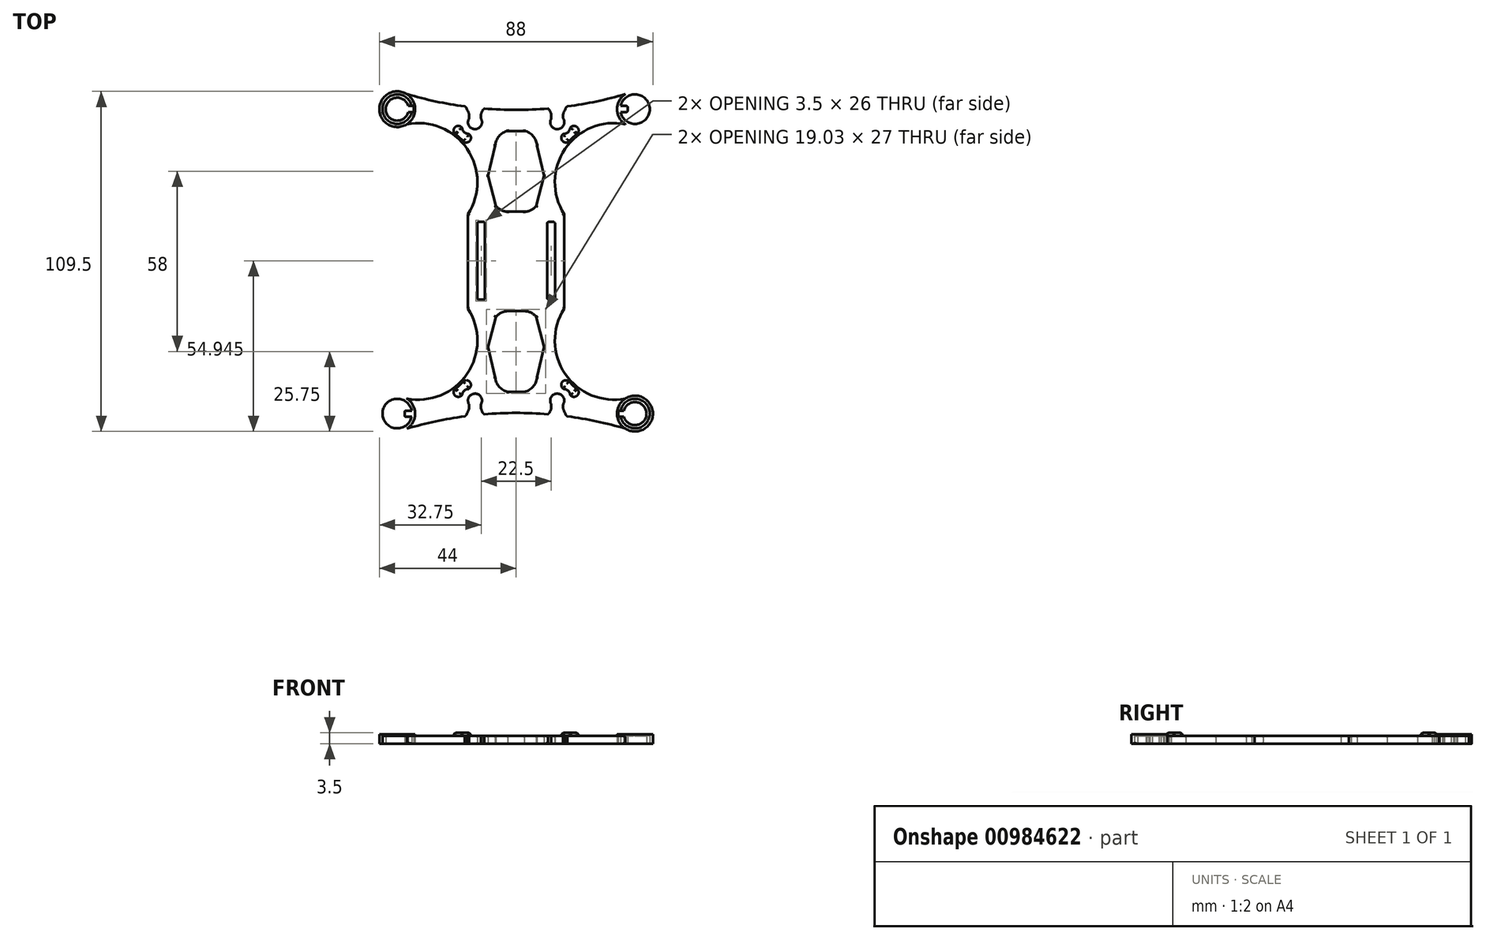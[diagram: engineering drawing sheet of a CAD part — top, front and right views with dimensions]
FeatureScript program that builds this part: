
annotation { "Feature Type Name" : "Feature", "Feature Type Description" : "" }
export const myFeature = defineFeature(function(context is Context, id is Id, definition is map)
    precondition{}
    {
        {
            var Q0;
            Q0=qCreatedBy(makeId("Top.planeOp"),FACE);
            var sketch = newSketch(context, id + "F0", { "sketchPlane" : qUnion([Q0])});
            skPoint(sketch, "E0.middle", {"position": v(0, 0) * mm});
            skCircle(sketch, "E1", {"center": v(-38.25, 49) * mm, "radius": 5.75 * mm});
            skCircle(sketch, "E2.MirrorC", {"center": v(38.25, 49) * mm, "radius": 5.75 * mm});
            skCircle(sketch, "E3.MirrorC", {"center": v(-38.25, -49) * mm, "radius": 5.75 * mm});
            skCircle(sketch, "E4.MirrorC", {"center": v(38.25, -49) * mm, "radius": 5.75 * mm});
            skArc(sketch, "E5", {"start": v(-35.12, 53.82) * mm, "mid": v(-25.9, 51.5) * mm, "end": v(-16.55, 49.89) * mm});
            skCircle(sketch, "E6", {"center": v(-38.25, 49) * mm, "radius": 3.7 * mm});
            skCircle(sketch, "E7.MirrorC", {"center": v(38.25, 49) * mm, "radius": 3.7 * mm});
            skCircle(sketch, "E8.MirrorC", {"center": v(38.25, -49) * mm, "radius": 3.7 * mm});
            skCircle(sketch, "E9.MirrorC", {"center": v(-38.25, -49) * mm, "radius": 3.7 * mm});
            skPoint(sketch, "E10.MirrorP", {"position": v(-9, -27.55) * mm});
            skArc(sketch, "E11.MirrorCS", {"start": v(-2.66, -42) * mm, "mid": v(-5.49, -40.33) * mm, "end": v(-6.7, -37.29) * mm});
            skArc(sketch, "E12.MirrorCS", {"start": v(-2.66, -16) * mm, "mid": v(-4.79, -16.51) * mm, "end": v(-6.5, -17.87) * mm});
            skLineSegment(sketch, "E13", {"start": v(-6.5, -17.87) * mm, "end": v(-9, -27.55) * mm});
            skLineSegment(sketch, "E14", {"start": v(-6.7, -37.29) * mm, "end": v(-9, -27.55) * mm});
            skArc(sketch, "E15.MirrorCS", {"start": v(2.66, -16) * mm, "mid": v(4.79, -16.51) * mm, "end": v(6.5, -17.87) * mm});
            skLineSegment(sketch, "E16.MirrorCS", {"start": v(6.5, -17.87) * mm, "end": v(9, -27.55) * mm});
            skLineSegment(sketch, "E17.MirrorCS", {"start": v(6.7, -37.29) * mm, "end": v(9, -27.55) * mm});
            skArc(sketch, "E18.MirrorCS", {"start": v(2.66, -42) * mm, "mid": v(5.49, -40.33) * mm, "end": v(6.7, -37.29) * mm});
            skLineSegment(sketch, "E19", {"start": v(-2.66, -16) * mm, "end": v(2.66, -16) * mm});
            skLineSegment(sketch, "E20", {"start": v(2.66, -42) * mm, "end": v(-2.66, -42) * mm});
            skLineSegment(sketch, "E21.MirrorCS", {"start": v(-2.66, 16) * mm, "end": v(2.66, 16) * mm});
            skArc(sketch, "E22.MirrorCS", {"start": v(-2.66, 16) * mm, "mid": v(-4.79, 16.51) * mm, "end": v(-6.5, 17.87) * mm});
            skLineSegment(sketch, "E23.MirrorCS", {"start": v(-6.5, 17.87) * mm, "end": v(-9, 27.55) * mm});
            skArc(sketch, "E24.MirrorCS", {"start": v(2.66, 16) * mm, "mid": v(4.79, 16.51) * mm, "end": v(6.5, 17.87) * mm});
            skLineSegment(sketch, "E25.MirrorCS", {"start": v(6.5, 17.87) * mm, "end": v(9, 27.55) * mm});
            skLineSegment(sketch, "E26.MirrorCS", {"start": v(-6.7, 37.29) * mm, "end": v(-9, 27.55) * mm});
            skLineSegment(sketch, "E27.MirrorCS", {"start": v(6.7, 37.29) * mm, "end": v(9, 27.55) * mm});
            skArc(sketch, "E28.MirrorCS", {"start": v(2.66, 42) * mm, "mid": v(5.49, 40.33) * mm, "end": v(6.7, 37.29) * mm});
            skLineSegment(sketch, "E29.MirrorCS", {"start": v(2.66, 42) * mm, "end": v(-2.66, 42) * mm});
            skArc(sketch, "E30.MirrorCS", {"start": v(-2.66, 42) * mm, "mid": v(-5.49, 40.33) * mm, "end": v(-6.7, 37.29) * mm});
            skArc(sketch, "E31", {"start": v(-15.5, 15.2) * mm, "mid": v(-15.74, 36.19) * mm, "end": v(-35.17, 44.14) * mm});
            skArc(sketch, "E32.MirrorCS", {"start": v(-35.12, -53.82) * mm, "mid": v(-25.9, -51.5) * mm, "end": v(-16.55, -49.89) * mm});
            skArc(sketch, "E33.MirrorCS", {"start": v(15.5, 15.2) * mm, "mid": v(15.74, 36.19) * mm, "end": v(35.17, 44.14) * mm});
            skArc(sketch, "E34.MirrorCS", {"start": v(15.5, -15.2) * mm, "mid": v(15.74, -36.19) * mm, "end": v(35.17, -44.14) * mm});
            skArc(sketch, "E35.MirrorCS", {"start": v(-15.5, -15.2) * mm, "mid": v(-15.74, -36.19) * mm, "end": v(-35.17, -44.14) * mm});
            skLineSegment(sketch, "E36", {"start": v(-15.5, -15.2) * mm, "end": v(-15.5, 15.2) * mm});
            skLineSegment(sketch, "E37.bottom", {"start": v(-12, -12.3) * mm, "end": v(-10.5, -12.3) * mm});
            skLineSegment(sketch, "E37.top", {"start": v(-12, 12.7) * mm, "end": v(-10.5, 12.7) * mm});
            skLineSegment(sketch, "E37.left", {"start": v(-12.5, -11.8) * mm, "end": v(-12.5, 12.2) * mm});
            skLineSegment(sketch, "E37.right", {"start": v(-10, -11.8) * mm, "end": v(-10, 12.2) * mm});
            skPoint(sketch, "E38.visualSharp", {"position": v(-10, -12.3) * mm});
            skArc(sketch, "E38.filletArc", {"start": v(-10.5, -12.3) * mm, "mid": v(-10.15, -12.16) * mm, "end": v(-10, -11.8) * mm});
            skPoint(sketch, "E39.visualSharp", {"position": v(-12.5, -12.3) * mm});
            skArc(sketch, "E39.filletArc", {"start": v(-12.5, -11.8) * mm, "mid": v(-12.35, -12.16) * mm, "end": v(-12, -12.3) * mm});
            skPoint(sketch, "E40.visualSharp", {"position": v(-10, 12.7) * mm});
            skArc(sketch, "E40.filletArc", {"start": v(-10, 12.2) * mm, "mid": v(-10.15, 12.55) * mm, "end": v(-10.5, 12.7) * mm});
            skPoint(sketch, "E41.visualSharp", {"position": v(-12.5, 12.7) * mm});
            skArc(sketch, "E41.filletArc", {"start": v(-12, 12.7) * mm, "mid": v(-12.35, 12.55) * mm, "end": v(-12.5, 12.2) * mm});
            skLineSegment(sketch, "E42.MirrorCS", {"start": v(12, -12.3) * mm, "end": v(10.5, -12.3) * mm});
            skArc(sketch, "E43.MirrorCS", {"start": v(12.5, -11.8) * mm, "mid": v(12.35, -12.16) * mm, "end": v(12, -12.3) * mm});
            skArc(sketch, "E44.MirrorCS", {"start": v(10.5, -12.3) * mm, "mid": v(10.15, -12.16) * mm, "end": v(10, -11.8) * mm});
            skLineSegment(sketch, "E45.MirrorCS", {"start": v(10, -11.8) * mm, "end": v(10, 12.2) * mm});
            skLineSegment(sketch, "E46.MirrorCS", {"start": v(12.5, -11.8) * mm, "end": v(12.5, 12.2) * mm});
            skArc(sketch, "E47.MirrorCS", {"start": v(10, 12.2) * mm, "mid": v(10.15, 12.55) * mm, "end": v(10.5, 12.7) * mm});
            skLineSegment(sketch, "E48.MirrorCS", {"start": v(12, 12.7) * mm, "end": v(10.5, 12.7) * mm});
            skArc(sketch, "E49.MirrorCS", {"start": v(12, 12.7) * mm, "mid": v(12.35, 12.55) * mm, "end": v(12.5, 12.2) * mm});
            skLineSegment(sketch, "E50", {"start": v(15.5, 15.2) * mm, "end": v(15.5, -15.2) * mm});
            skArc(sketch, "E51.trimOffspring", {"start": v(-10.28, 49.21) * mm, "mid": v(0, 48.79) * mm, "end": v(10.28, 49.21) * mm});
            skArc(sketch, "E52", {"start": v(-15.18, 45.95) * mm, "mid": v(-13.3, 42.57) * mm, "end": v(-11.24, 45.85) * mm});
            skArc(sketch, "E53", {"start": v(-15.18, 45.95) * mm, "mid": v(-15.18, 47.49) * mm, "end": v(-15.83, 48.88) * mm});
            skArc(sketch, "E54.MirrorCS", {"start": v(-11.24, 45.85) * mm, "mid": v(-11.2, 47.66) * mm, "end": v(-10.28, 49.21) * mm});
            skArc(sketch, "E55.trimOffspring", {"start": v(16.55, 49.89) * mm, "mid": v(25.9, 51.5) * mm, "end": v(35.12, 53.82) * mm});
            skArc(sketch, "E56.trimOffspring", {"start": v(-10.28, -49.21) * mm, "mid": v(0, -48.79) * mm, "end": v(10.28, -49.21) * mm});
            skArc(sketch, "E57.trimOffspring", {"start": v(16.55, -49.89) * mm, "mid": v(25.9, -51.5) * mm, "end": v(35.12, -53.82) * mm});
            skArc(sketch, "E58.MirrorCS", {"start": v(11.24, 45.85) * mm, "mid": v(11.2, 47.66) * mm, "end": v(10.28, 49.21) * mm});
            skArc(sketch, "E59.MirrorCS", {"start": v(15.18, 45.95) * mm, "mid": v(15.18, 47.49) * mm, "end": v(15.83, 48.88) * mm});
            skArc(sketch, "E60.MirrorCS", {"start": v(15.18, 45.95) * mm, "mid": v(13.3, 42.57) * mm, "end": v(11.24, 45.85) * mm});
            skArc(sketch, "E61.MirrorCS", {"start": v(15.18, -45.95) * mm, "mid": v(13.3, -42.57) * mm, "end": v(11.24, -45.85) * mm});
            skArc(sketch, "E62.MirrorCS", {"start": v(11.24, -45.85) * mm, "mid": v(11.2, -47.66) * mm, "end": v(10.28, -49.21) * mm});
            skArc(sketch, "E63.MirrorCS", {"start": v(15.18, -45.95) * mm, "mid": v(15.18, -47.49) * mm, "end": v(15.83, -48.88) * mm});
            skArc(sketch, "E64.MirrorCS", {"start": v(-11.24, -45.85) * mm, "mid": v(-11.2, -47.66) * mm, "end": v(-10.28, -49.21) * mm});
            skArc(sketch, "E65.MirrorCS", {"start": v(-15.18, -45.95) * mm, "mid": v(-15.18, -47.49) * mm, "end": v(-15.83, -48.88) * mm});
            skArc(sketch, "E66.MirrorCS", {"start": v(-15.18, -45.95) * mm, "mid": v(-13.3, -42.57) * mm, "end": v(-11.24, -45.85) * mm});
            skArc(sketch, "E67", {"start": v(16.55, 49.89) * mm, "mid": v(16.05, 49.49) * mm, "end": v(15.83, 48.88) * mm});
            skArc(sketch, "E68.MirrorCS", {"start": v(-16.55, 49.89) * mm, "mid": v(-16.05, 49.49) * mm, "end": v(-15.83, 48.88) * mm});
            skArc(sketch, "E69.MirrorCS", {"start": v(-16.55, -49.89) * mm, "mid": v(-16.05, -49.49) * mm, "end": v(-15.83, -48.88) * mm});
            skArc(sketch, "E70.MirrorCS", {"start": v(16.55, -49.89) * mm, "mid": v(16.05, -49.49) * mm, "end": v(15.83, -48.88) * mm});
            skCircle(sketch, "E71", {"center": v(-38.25, 49) * mm, "radius": 4.75 * mm});
            skCircle(sketch, "E72.MirrorC", {"center": v(38.25, 49) * mm, "radius": 4.75 * mm});
            skCircle(sketch, "E73.MirrorC", {"center": v(38.25, -49) * mm, "radius": 4.75 * mm});
            skCircle(sketch, "E74.MirrorC", {"center": v(-38.25, -49) * mm, "radius": 4.75 * mm});
            skSolve(sketch);
        }
        {
            var Q0;
            {var subQ4=sQuery(id+"F0.wireOp",EDGE,"E5");Q0=makeQuery(id+"F0.imprint","IMPRINT",FACE,{"disambiguationData":[TD([[makeQuery(id+"F0.imprint","IMPRINT",EDGE,{"derivedFrom":subQ4}),-1.0]])]});}
            var Q1;
            Q1=makeQuery(id+"F0.imprint","IMPRINT",FACE,{"disambiguationData":[TD([[makeQuery(id+"F0.imprint","IMPRINT",EDGE,{"derivedFrom":sQuery(id+"F0.wireOp",EDGE,"E9.MirrorC")}),1.0]])]});
            var Q2;
            Q2=makeQuery(id+"F0.imprint","IMPRINT",FACE,{"disambiguationData":[TD([[makeQuery(id+"F0.imprint","IMPRINT",EDGE,{"derivedFrom":sQuery(id+"F0.wireOp",EDGE,"E8.MirrorC")}),-1.0]])]});
            var Q3;
            Q3=makeQuery(id+"F0.imprint","IMPRINT",FACE,{"disambiguationData":[TD([[makeQuery(id+"F0.imprint","IMPRINT",EDGE,{"derivedFrom":sQuery(id+"F0.wireOp",EDGE,"E6")}),-1.0]])]});
            var Q4;
            Q4=makeQuery(id+"F0.imprint","IMPRINT",FACE,{"disambiguationData":[TD([[makeQuery(id+"F0.imprint","IMPRINT",EDGE,{"derivedFrom":sQuery(id+"F0.wireOp",EDGE,"E7.MirrorC")}),1.0]])]});
            var Q5;
            {var subQ0=sQuery(id+"F0.wireOp",EDGE,"7a08c846-7200-404a-ab22-a396ae0e95b40.MirrorCS");Q5=makeQuery(id+"F0.imprint","IMPRINT",FACE,{"disambiguationData":[TD([[makeQuery(id+"F0.imprint","IMPRINT",EDGE,{"derivedFrom":subQ0}),-1.0]])]});}
            extrude(context, id + "F1", {"entities" : qUnion([Q0, Q1, Q2, Q3, Q4, Q5]), "depth" : 2.5 * mm});
        }
        {
            var Q0;
            Q0=makeQuery(id+"F0.imprint","IMPRINT",FACE,{"disambiguationData":[TD([[makeQuery(id+"F0.imprint","IMPRINT",EDGE,{"derivedFrom":sQuery(id+"F0.wireOp",EDGE,"E71")}),-1.0]])]});
            var Q1;
            Q1=makeQuery(id+"F0.imprint","IMPRINT",FACE,{"disambiguationData":[TD([[makeQuery(id+"F0.imprint","IMPRINT",EDGE,{"derivedFrom":sQuery(id+"F0.wireOp",EDGE,"E72.MirrorC")}),1.0]])]});
            var Q2;
            Q2=makeQuery(id+"F0.imprint","IMPRINT",FACE,{"disambiguationData":[TD([[makeQuery(id+"F0.imprint","IMPRINT",EDGE,{"derivedFrom":sQuery(id+"F0.wireOp",EDGE,"E74.MirrorC")}),1.0]])]});
            var Q3;
            Q3=makeQuery(id+"F0.imprint","IMPRINT",FACE,{"disambiguationData":[TD([[makeQuery(id+"F0.imprint","IMPRINT",EDGE,{"derivedFrom":sQuery(id+"F0.wireOp",EDGE,"E73.MirrorC")}),-1.0]])]});
            extrude(context, id + "F2", {"entities" : qUnion([Q0, Q1, Q2, Q3]), "operationType" : NewBodyOperationType.ADD, "depth" : 3 * mm});
        }
        {
            var Q0;
            Q0=makeQuery(id+"F0.imprint","IMPRINT",FACE,{"disambiguationData":[TD([[makeQuery(id+"F0.imprint","IMPRINT",EDGE,{"derivedFrom":sQuery(id+"F0.wireOp",EDGE,"E6")}),1.0]])]});
            var Q1;
            Q1=makeQuery(id+"F0.imprint","IMPRINT",FACE,{"disambiguationData":[TD([[makeQuery(id+"F0.imprint","IMPRINT",EDGE,{"derivedFrom":sQuery(id+"F0.wireOp",EDGE,"E7.MirrorC")}),-1.0]])]});
            var Q2;
            Q2=makeQuery(id+"F0.imprint","IMPRINT",FACE,{"disambiguationData":[TD([[makeQuery(id+"F0.imprint","IMPRINT",EDGE,{"derivedFrom":sQuery(id+"F0.wireOp",EDGE,"E9.MirrorC")}),-1.0]])]});
            var Q3;
            Q3=makeQuery(id+"F0.imprint","IMPRINT",FACE,{"disambiguationData":[TD([[makeQuery(id+"F0.imprint","IMPRINT",EDGE,{"derivedFrom":sQuery(id+"F0.wireOp",EDGE,"E8.MirrorC")}),1.0]])]});
            extrude(context, id + "F3", {"entities" : qUnion([Q0, Q1, Q2, Q3]), "operationType" : NewBodyOperationType.REMOVE, "depth" : 6.5 * mm, "hasSecondDirection" : true, "secondDirectionOppositeDirection" : false, "secondDirectionDepth" : 2.5 * mm});
        }
        {
            var Q0;
            Q0=makeQuery(id+"F0.imprint","IMPRINT",FACE,{"disambiguationData":[TD([[makeQuery(id+"F0.imprint","IMPRINT",EDGE,{"derivedFrom":sQuery(id+"F0.wireOp",EDGE,"E6")}),-1.0]])]});
            var sketch = newSketch(context, id + "F4", { "sketchPlane" : qUnion([Q0])});
            skLineSegment(sketch, "E75.bottom", {"start": v(-33.4, 50.05) * mm, "end": v(-35.4, 50.05) * mm});
            skLineSegment(sketch, "E75.top", {"start": v(-33.4, 48.05) * mm, "end": v(-35.4, 48.05) * mm});
            skLineSegment(sketch, "E75.left", {"start": v(-32.9, 49.55) * mm, "end": v(-32.9, 48.55) * mm});
            skLineSegment(sketch, "E75.right", {"start": v(-35.9, 49.55) * mm, "end": v(-35.9, 48.55) * mm});
            skPoint(sketch, "E75.middle", {"position": v(-34.4, 49.05) * mm});
            skPoint(sketch, "E76.visualSharp", {"position": v(-32.9, 50.05) * mm});
            skArc(sketch, "E76.filletArc", {"start": v(-32.9, 49.55) * mm, "mid": v(-33.05, 49.9) * mm, "end": v(-33.4, 50.05) * mm});
            skPoint(sketch, "E77.visualSharp", {"position": v(-32.9, 48.05) * mm});
            skArc(sketch, "E77.filletArc", {"start": v(-33.4, 48.05) * mm, "mid": v(-33.05, 48.2) * mm, "end": v(-32.9, 48.55) * mm});
            skPoint(sketch, "E78.visualSharp", {"position": v(-35.9, 48.05) * mm});
            skArc(sketch, "E78.filletArc", {"start": v(-35.9, 48.55) * mm, "mid": v(-35.75, 48.2) * mm, "end": v(-35.4, 48.05) * mm});
            skPoint(sketch, "E79.visualSharp", {"position": v(-35.9, 50.05) * mm});
            skArc(sketch, "E79.filletArc", {"start": v(-35.4, 50.05) * mm, "mid": v(-35.75, 49.9) * mm, "end": v(-35.9, 49.55) * mm});
            skLineSegment(sketch, "E80.MirrorCS", {"start": v(33.4, 48.05) * mm, "end": v(35.4, 48.05) * mm});
            skLineSegment(sketch, "E81.MirrorCS", {"start": v(35.9, 49.55) * mm, "end": v(35.9, 48.55) * mm});
            skLineSegment(sketch, "E82.MirrorCS", {"start": v(33.4, 50.05) * mm, "end": v(35.4, 50.05) * mm});
            skLineSegment(sketch, "E83.MirrorCS", {"start": v(32.9, 49.55) * mm, "end": v(32.9, 48.55) * mm});
            skArc(sketch, "E84.MirrorCS", {"start": v(32.9, 49.55) * mm, "mid": v(33.05, 49.9) * mm, "end": v(33.4, 50.05) * mm});
            skArc(sketch, "E85.MirrorCS", {"start": v(33.4, 48.05) * mm, "mid": v(33.05, 48.2) * mm, "end": v(32.9, 48.55) * mm});
            skArc(sketch, "E86.MirrorCS", {"start": v(35.9, 48.55) * mm, "mid": v(35.75, 48.2) * mm, "end": v(35.4, 48.05) * mm});
            skArc(sketch, "E87.MirrorCS", {"start": v(35.4, 50.05) * mm, "mid": v(35.75, 49.9) * mm, "end": v(35.9, 49.55) * mm});
            skLineSegment(sketch, "E88.MirrorCS", {"start": v(33.4, -48.05) * mm, "end": v(35.4, -48.05) * mm});
            skLineSegment(sketch, "E89.MirrorCS", {"start": v(33.4, -50.05) * mm, "end": v(35.4, -50.05) * mm});
            skLineSegment(sketch, "E90.MirrorCS", {"start": v(32.9, -49.55) * mm, "end": v(32.9, -48.55) * mm});
            skLineSegment(sketch, "E91.MirrorCS", {"start": v(35.9, -49.55) * mm, "end": v(35.9, -48.55) * mm});
            skArc(sketch, "E92.MirrorCS", {"start": v(35.4, -50.05) * mm, "mid": v(35.75, -49.9) * mm, "end": v(35.9, -49.55) * mm});
            skArc(sketch, "E93.MirrorCS", {"start": v(32.9, -49.55) * mm, "mid": v(33.05, -49.9) * mm, "end": v(33.4, -50.05) * mm});
            skArc(sketch, "E94.MirrorCS", {"start": v(33.4, -48.05) * mm, "mid": v(33.05, -48.2) * mm, "end": v(32.9, -48.55) * mm});
            skArc(sketch, "E95.MirrorCS", {"start": v(35.9, -48.55) * mm, "mid": v(35.75, -48.2) * mm, "end": v(35.4, -48.05) * mm});
            skLineSegment(sketch, "E96.MirrorCS", {"start": v(-33.4, -48.05) * mm, "end": v(-35.4, -48.05) * mm});
            skArc(sketch, "E97.MirrorCS", {"start": v(-35.9, -48.55) * mm, "mid": v(-35.75, -48.2) * mm, "end": v(-35.4, -48.05) * mm});
            skLineSegment(sketch, "E98.MirrorCS", {"start": v(-35.9, -49.55) * mm, "end": v(-35.9, -48.55) * mm});
            skArc(sketch, "E99.MirrorCS", {"start": v(-35.4, -50.05) * mm, "mid": v(-35.75, -49.9) * mm, "end": v(-35.9, -49.55) * mm});
            skLineSegment(sketch, "E100.MirrorCS", {"start": v(-33.4, -50.05) * mm, "end": v(-35.4, -50.05) * mm});
            skArc(sketch, "E101.MirrorCS", {"start": v(-32.9, -49.55) * mm, "mid": v(-33.05, -49.9) * mm, "end": v(-33.4, -50.05) * mm});
            skLineSegment(sketch, "E102.MirrorCS", {"start": v(-32.9, -49.55) * mm, "end": v(-32.9, -48.55) * mm});
            skArc(sketch, "E103.MirrorCS", {"start": v(-33.4, -48.05) * mm, "mid": v(-33.05, -48.2) * mm, "end": v(-32.9, -48.55) * mm});
            skSolve(sketch);
        }
        {
            var Q0;
            Q0=qSketchRegion(id+"F4",true);
            extrude(context, id + "F5", {"entities" : qUnion([Q0]), "operationType" : NewBodyOperationType.REMOVE, "depth" : 4 * mm});
        }
        {
            var Q0;
            Q0=makeQuery(id+"F1.opExtrude","CAP_EDGE",EDGE,{"disambiguationData":[OSD([sQuery(id+"F0.wireOp",EDGE,"E23.MirrorCS")])],"isStart":true});
            var Q1;
            Q1=makeQuery(id+"F1.opExtrude","CAP_EDGE",EDGE,{"disambiguationData":[OSD([sQuery(id+"F0.wireOp",EDGE,"E22.MirrorCS")])],"isStart":true});
            var Q2;
            Q2=makeQuery(id+"F1.opExtrude","CAP_EDGE",EDGE,{"disambiguationData":[OSD([sQuery(id+"F0.wireOp",EDGE,"E21.MirrorCS")])],"isStart":true});
            var Q3;
            Q3=makeQuery(id+"F1.opExtrude","CAP_EDGE",EDGE,{"disambiguationData":[OSD([sQuery(id+"F0.wireOp",EDGE,"E25.MirrorCS")])],"isStart":true});
            var Q4;
            Q4=makeQuery(id+"F1.opExtrude","CAP_EDGE",EDGE,{"disambiguationData":[OSD([sQuery(id+"F0.wireOp",EDGE,"E24.MirrorCS")])],"isStart":true});
            var Q5;
            Q5=makeQuery(id+"F1.opExtrude","CAP_EDGE",EDGE,{"disambiguationData":[OSD([sQuery(id+"F0.wireOp",EDGE,"E27.MirrorCS")])],"isStart":true});
            var Q6;
            Q6=makeQuery(id+"F1.opExtrude","CAP_EDGE",EDGE,{"disambiguationData":[OSD([sQuery(id+"F0.wireOp",EDGE,"E26.MirrorCS")])],"isStart":true});
            var Q7;
            Q7=makeQuery(id+"F1.opExtrude","CAP_EDGE",EDGE,{"disambiguationData":[OSD([sQuery(id+"F0.wireOp",EDGE,"E30.MirrorCS")])],"isStart":true});
            var Q8;
            Q8=makeQuery(id+"F1.opExtrude","CAP_EDGE",EDGE,{"disambiguationData":[OSD([sQuery(id+"F0.wireOp",EDGE,"E29.MirrorCS")])],"isStart":true});
            var Q9;
            Q9=makeQuery(id+"F1.opExtrude","CAP_EDGE",EDGE,{"disambiguationData":[OSD([sQuery(id+"F0.wireOp",EDGE,"E28.MirrorCS")])],"isStart":true});
            var Q10;
            Q10=makeQuery(id+"F1.opExtrude","CAP_EDGE",EDGE,{"disambiguationData":[OSD([sQuery(id+"F0.wireOp",EDGE,"E24.MirrorCS")])],"isStart":false});
            var Q11;
            Q11=makeQuery(id+"F1.opExtrude","CAP_EDGE",EDGE,{"disambiguationData":[OSD([sQuery(id+"F0.wireOp",EDGE,"E21.MirrorCS")])],"isStart":false});
            var Q12;
            Q12=makeQuery(id+"F1.opExtrude","CAP_EDGE",EDGE,{"disambiguationData":[OSD([sQuery(id+"F0.wireOp",EDGE,"E22.MirrorCS")])],"isStart":false});
            var Q13;
            Q13=makeQuery(id+"F1.opExtrude","CAP_EDGE",EDGE,{"disambiguationData":[OSD([sQuery(id+"F0.wireOp",EDGE,"E23.MirrorCS")])],"isStart":false});
            var Q14;
            Q14=makeQuery(id+"F1.opExtrude","CAP_EDGE",EDGE,{"disambiguationData":[OSD([sQuery(id+"F0.wireOp",EDGE,"E26.MirrorCS")])],"isStart":false});
            var Q15;
            Q15=makeQuery(id+"F1.opExtrude","CAP_EDGE",EDGE,{"disambiguationData":[OSD([sQuery(id+"F0.wireOp",EDGE,"E30.MirrorCS")])],"isStart":false});
            var Q16;
            Q16=makeQuery(id+"F1.opExtrude","CAP_EDGE",EDGE,{"disambiguationData":[OSD([sQuery(id+"F0.wireOp",EDGE,"E29.MirrorCS")])],"isStart":false});
            var Q17;
            Q17=makeQuery(id+"F1.opExtrude","CAP_EDGE",EDGE,{"disambiguationData":[OSD([sQuery(id+"F0.wireOp",EDGE,"E28.MirrorCS")])],"isStart":false});
            var Q18;
            Q18=makeQuery(id+"F1.opExtrude","CAP_EDGE",EDGE,{"disambiguationData":[OSD([sQuery(id+"F0.wireOp",EDGE,"E27.MirrorCS")])],"isStart":false});
            var Q19;
            Q19=makeQuery(id+"F1.opExtrude","CAP_EDGE",EDGE,{"disambiguationData":[OSD([sQuery(id+"F0.wireOp",EDGE,"E25.MirrorCS")])],"isStart":false});
            var Q20;
            Q20=makeQuery(id+"F1.opExtrude","CAP_EDGE",EDGE,{"disambiguationData":[OSD([sQuery(id+"F0.wireOp",EDGE,"E20")])],"isStart":true});
            var Q21;
            Q21=makeQuery(id+"F1.opExtrude","CAP_EDGE",EDGE,{"disambiguationData":[OSD([sQuery(id+"F0.wireOp",EDGE,"E11.MirrorCS")])],"isStart":true});
            var Q22;
            Q22=makeQuery(id+"F1.opExtrude","CAP_EDGE",EDGE,{"disambiguationData":[OSD([sQuery(id+"F0.wireOp",EDGE,"E14")])],"isStart":true});
            var Q23;
            Q23=makeQuery(id+"F1.opExtrude","CAP_EDGE",EDGE,{"disambiguationData":[OSD([sQuery(id+"F0.wireOp",EDGE,"E13")])],"isStart":true});
            var Q24;
            Q24=makeQuery(id+"F1.opExtrude","CAP_EDGE",EDGE,{"disambiguationData":[OSD([sQuery(id+"F0.wireOp",EDGE,"E12.MirrorCS")])],"isStart":true});
            var Q25;
            Q25=makeQuery(id+"F1.opExtrude","CAP_EDGE",EDGE,{"disambiguationData":[OSD([sQuery(id+"F0.wireOp",EDGE,"E19")])],"isStart":true});
            var Q26;
            Q26=makeQuery(id+"F1.opExtrude","CAP_EDGE",EDGE,{"disambiguationData":[OSD([sQuery(id+"F0.wireOp",EDGE,"E15.MirrorCS")])],"isStart":true});
            var Q27;
            Q27=makeQuery(id+"F1.opExtrude","CAP_EDGE",EDGE,{"disambiguationData":[OSD([sQuery(id+"F0.wireOp",EDGE,"E16.MirrorCS")])],"isStart":true});
            var Q28;
            Q28=makeQuery(id+"F1.opExtrude","CAP_EDGE",EDGE,{"disambiguationData":[OSD([sQuery(id+"F0.wireOp",EDGE,"E17.MirrorCS")])],"isStart":true});
            var Q29;
            Q29=makeQuery(id+"F1.opExtrude","CAP_EDGE",EDGE,{"disambiguationData":[OSD([sQuery(id+"F0.wireOp",EDGE,"E18.MirrorCS")])],"isStart":true});
            var Q30;
            Q30=makeQuery(id+"F1.opExtrude","CAP_EDGE",EDGE,{"disambiguationData":[OSD([sQuery(id+"F0.wireOp",EDGE,"E20")])],"isStart":false});
            var Q31;
            Q31=makeQuery(id+"F1.opExtrude","CAP_EDGE",EDGE,{"disambiguationData":[OSD([sQuery(id+"F0.wireOp",EDGE,"E11.MirrorCS")])],"isStart":false});
            var Q32;
            Q32=makeQuery(id+"F1.opExtrude","CAP_EDGE",EDGE,{"disambiguationData":[OSD([sQuery(id+"F0.wireOp",EDGE,"E14")])],"isStart":false});
            var Q33;
            Q33=makeQuery(id+"F1.opExtrude","CAP_EDGE",EDGE,{"disambiguationData":[OSD([sQuery(id+"F0.wireOp",EDGE,"E13")])],"isStart":false});
            var Q34;
            Q34=makeQuery(id+"F1.opExtrude","CAP_EDGE",EDGE,{"disambiguationData":[OSD([sQuery(id+"F0.wireOp",EDGE,"E18.MirrorCS")])],"isStart":false});
            var Q35;
            Q35=makeQuery(id+"F1.opExtrude","CAP_EDGE",EDGE,{"disambiguationData":[OSD([sQuery(id+"F0.wireOp",EDGE,"E17.MirrorCS")])],"isStart":false});
            var Q36;
            Q36=makeQuery(id+"F1.opExtrude","CAP_EDGE",EDGE,{"disambiguationData":[OSD([sQuery(id+"F0.wireOp",EDGE,"E12.MirrorCS")])],"isStart":false});
            var Q37;
            Q37=makeQuery(id+"F1.opExtrude","CAP_EDGE",EDGE,{"disambiguationData":[OSD([sQuery(id+"F0.wireOp",EDGE,"E19")])],"isStart":false});
            var Q38;
            Q38=makeQuery(id+"F1.opExtrude","CAP_EDGE",EDGE,{"disambiguationData":[OSD([sQuery(id+"F0.wireOp",EDGE,"E15.MirrorCS")])],"isStart":false});
            var Q39;
            Q39=makeQuery(id+"F1.opExtrude","CAP_EDGE",EDGE,{"disambiguationData":[OSD([sQuery(id+"F0.wireOp",EDGE,"E16.MirrorCS")])],"isStart":false});
            fillet(context, id + "F6", {"entities" : qUnion([Q0, Q1, Q2, Q3, Q4, Q5, Q6, Q7, Q8, Q9, Q10, Q11, Q12, Q13, Q14, Q15, Q16, Q17, Q18, Q19, Q20, Q21, Q22, Q23, Q24, Q25, Q26, Q27, Q28, Q29, Q30, Q31, Q32, Q33, Q34, Q35, Q36, Q37, Q38, Q39]), "radius" : .5 * mm, "tangentPropagation" : true, "allowEdgeOverflow" : false});
        }
        {
            var Q0;
            Q0=makeQuery(id+"F1.opExtrude","CAP_EDGE",EDGE,{"disambiguationData":[OSD([sQuery(id+"F0.wireOp",EDGE,"E37.left")])],"isStart":false});
            var Q1;
            Q1=makeQuery(id+"F1.opExtrude","CAP_EDGE",EDGE,{"disambiguationData":[OSD([sQuery(id+"F0.wireOp",EDGE,"E37.right")])],"isStart":false});
            var Q2;
            Q2=makeQuery(id+"F1.opExtrude","CAP_EDGE",EDGE,{"disambiguationData":[OSD([sQuery(id+"F0.wireOp",EDGE,"E45.MirrorCS")])],"isStart":false});
            var Q3;
            Q3=makeQuery(id+"F1.opExtrude","CAP_EDGE",EDGE,{"disambiguationData":[OSD([sQuery(id+"F0.wireOp",EDGE,"E46.MirrorCS")])],"isStart":false});
            var Q4;
            Q4=makeQuery(id+"F1.opExtrude","CAP_EDGE",EDGE,{"disambiguationData":[OSD([sQuery(id+"F0.wireOp",EDGE,"E37.left")])],"isStart":true});
            var Q5;
            Q5=makeQuery(id+"F1.opExtrude","CAP_EDGE",EDGE,{"disambiguationData":[OSD([sQuery(id+"F0.wireOp",EDGE,"E37.right")])],"isStart":true});
            var Q6;
            Q6=makeQuery(id+"F1.opExtrude","CAP_EDGE",EDGE,{"disambiguationData":[OSD([sQuery(id+"F0.wireOp",EDGE,"E45.MirrorCS")])],"isStart":true});
            var Q7;
            Q7=makeQuery(id+"F1.opExtrude","CAP_EDGE",EDGE,{"disambiguationData":[OSD([sQuery(id+"F0.wireOp",EDGE,"E46.MirrorCS")])],"isStart":true});
            fillet(context, id + "F7", {"entities" : qUnion([Q0, Q1, Q2, Q3, Q4, Q5, Q6, Q7]), "radius" : .5 * mm, "tangentPropagation" : true, "allowEdgeOverflow" : false});
        }
        {
            var Q0;
            Q0=makeQuery(id+"F1.opExtrude","CAP_EDGE",EDGE,{"disambiguationData":[OSD([sQuery(id+"F0.wireOp",EDGE,"E9.MirrorC")])],"isStart":true});
            var Q1;
            Q1=makeQuery(id+"F1.opExtrude","CAP_EDGE",EDGE,{"disambiguationData":[OSD([sQuery(id+"F0.wireOp",EDGE,"E8.MirrorC")])],"isStart":true});
            var Q2;
            Q2=makeQuery(id+"F1.opExtrude","CAP_EDGE",EDGE,{"disambiguationData":[OSD([sQuery(id+"F0.wireOp",EDGE,"E7.MirrorC")])],"isStart":true});
            var Q3;
            Q3=makeQuery(id+"F1.opExtrude","CAP_EDGE",EDGE,{"disambiguationData":[OSD([sQuery(id+"F0.wireOp",EDGE,"E6")])],"isStart":true});
            fillet(context, id + "F8", {"entities" : qUnion([Q0, Q1, Q2, Q3]), "radius" : .5 * mm, "tangentPropagation" : true, "allowEdgeOverflow" : false});
        }
        {
            var Q0;
            Q0=makeQuery(id+"F1.opExtrude","CAP_EDGE",EDGE,{"disambiguationData":[OSD([sQuery(id+"F0.wireOp",EDGE,"E36")])],"isStart":false});
            var Q1;
            Q1=makeQuery(id+"F1.opExtrude","CAP_EDGE",EDGE,{"disambiguationData":[OSD([sQuery(id+"F0.wireOp",EDGE,"E31")])],"isStart":false});
            var Q2;
            Q2=makeQuery(id+"F1.opExtrude","CAP_EDGE",EDGE,{"disambiguationData":[OSD([sQuery(id+"F0.wireOp",EDGE,"E5")])],"isStart":false});
            var Q3;
            Q3=makeQuery(id+"F1.opExtrude","CAP_EDGE",EDGE,{"disambiguationData":[OSD([sQuery(id+"F0.wireOp",EDGE,"E51.trimOffspring")])],"isStart":false});
            var Q4;
            Q4=makeQuery(id+"F1.opExtrude","CAP_EDGE",EDGE,{"disambiguationData":[OSD([sQuery(id+"F0.wireOp",EDGE,"E55.trimOffspring")])],"isStart":false});
            var Q5;
            Q5=makeQuery(id+"F1.opExtrude","CAP_EDGE",EDGE,{"disambiguationData":[OSD([sQuery(id+"F0.wireOp",EDGE,"E33.MirrorCS")])],"isStart":false});
            var Q6;
            Q6=makeQuery(id+"F1.opExtrude","CAP_EDGE",EDGE,{"disambiguationData":[OSD([sQuery(id+"F0.wireOp",EDGE,"E50")])],"isStart":false});
            var Q7;
            Q7=makeQuery(id+"F1.opExtrude","CAP_EDGE",EDGE,{"disambiguationData":[OSD([sQuery(id+"F0.wireOp",EDGE,"E35.MirrorCS")])],"isStart":false});
            var Q8;
            Q8=makeQuery(id+"F1.opExtrude","CAP_EDGE",EDGE,{"disambiguationData":[OSD([sQuery(id+"F0.wireOp",EDGE,"E34.MirrorCS")])],"isStart":false});
            var Q9;
            Q9=makeQuery(id+"F1.opExtrude","CAP_EDGE",EDGE,{"disambiguationData":[OSD([sQuery(id+"F0.wireOp",EDGE,"E57.trimOffspring")])],"isStart":false});
            var Q10;
            Q10=makeQuery(id+"F1.opExtrude","CAP_EDGE",EDGE,{"disambiguationData":[OSD([sQuery(id+"F0.wireOp",EDGE,"E56.trimOffspring")])],"isStart":false});
            var Q11;
            Q11=makeQuery(id+"F1.opExtrude","CAP_EDGE",EDGE,{"disambiguationData":[OSD([sQuery(id+"F0.wireOp",EDGE,"E32.MirrorCS")])],"isStart":false});
            var Q12;
            Q12=makeQuery(id+"F1.opExtrude","CAP_EDGE",EDGE,{"disambiguationData":[OSD([sQuery(id+"F0.wireOp",EDGE,"E35.MirrorCS")])],"isStart":true});
            var Q13;
            Q13=makeQuery(id+"F1.opExtrude","CAP_EDGE",EDGE,{"disambiguationData":[OSD([sQuery(id+"F0.wireOp",EDGE,"E32.MirrorCS")])],"isStart":true});
            var Q14;
            Q14=makeQuery(id+"F1.opExtrude","CAP_EDGE",EDGE,{"disambiguationData":[OSD([sQuery(id+"F0.wireOp",EDGE,"E56.trimOffspring")])],"isStart":true});
            var Q15;
            Q15=makeQuery(id+"F1.opExtrude","CAP_EDGE",EDGE,{"disambiguationData":[OSD([sQuery(id+"F0.wireOp",EDGE,"E57.trimOffspring")])],"isStart":true});
            var Q16;
            Q16=makeQuery(id+"F1.opExtrude","CAP_EDGE",EDGE,{"disambiguationData":[OSD([sQuery(id+"F0.wireOp",EDGE,"E3.MirrorC")])],"isStart":true});
            var Q17;
            Q17=makeQuery(id+"F1.opExtrude","CAP_EDGE",EDGE,{"disambiguationData":[OSD([sQuery(id+"F0.wireOp",EDGE,"E34.MirrorCS")])],"isStart":true});
            var Q18;
            Q18=makeQuery(id+"F1.opExtrude","CAP_EDGE",EDGE,{"disambiguationData":[OSD([sQuery(id+"F0.wireOp",EDGE,"E4.MirrorC")])],"isStart":true});
            var Q19;
            {var subQ0=sQuery(id+"F0.wireOp",EDGE,"E37.left");Q19=makeQuery(id+"F7.opFillet","BLEND_EDGE",EDGE,{"blendedFrom":[makeQuery(id+"F1.opExtrude","CAP_EDGE",EDGE,{"disambiguationData":[OSD([subQ0])],"isStart":true}),makeQuery(id+"F1.opExtrude","CAP_FACE",FACE,{"disambiguationData":[OSD([sQuery(id+"F0.wireOp",EDGE,"E1"),sQuery(id+"F0.wireOp",EDGE,"E2.MirrorC"),sQuery(id+"F0.wireOp",EDGE,"E3.MirrorC"),sQuery(id+"F0.wireOp",EDGE,"E4.MirrorC"),sQuery(id+"F0.wireOp",EDGE,"E5"),sQuery(id+"F0.wireOp",EDGE,"E6"),sQuery(id+"F0.wireOp",EDGE,"E7.MirrorC"),sQuery(id+"F0.wireOp",EDGE,"E8.MirrorC"),sQuery(id+"F0.wireOp",EDGE,"E9.MirrorC"),sQuery(id+"F0.wireOp",EDGE,"E11.MirrorCS"),sQuery(id+"F0.wireOp",EDGE,"E12.MirrorCS"),sQuery(id+"F0.wireOp",EDGE,"E13"),sQuery(id+"F0.wireOp",EDGE,"E14"),sQuery(id+"F0.wireOp",EDGE,"E15.MirrorCS"),sQuery(id+"F0.wireOp",EDGE,"E16.MirrorCS"),sQuery(id+"F0.wireOp",EDGE,"E17.MirrorCS"),sQuery(id+"F0.wireOp",EDGE,"E18.MirrorCS"),sQuery(id+"F0.wireOp",EDGE,"E19"),sQuery(id+"F0.wireOp",EDGE,"E20"),sQuery(id+"F0.wireOp",EDGE,"E21.MirrorCS"),sQuery(id+"F0.wireOp",EDGE,"E22.MirrorCS"),sQuery(id+"F0.wireOp",EDGE,"E23.MirrorCS"),sQuery(id+"F0.wireOp",EDGE,"E24.MirrorCS"),sQuery(id+"F0.wireOp",EDGE,"E25.MirrorCS"),sQuery(id+"F0.wireOp",EDGE,"E26.MirrorCS"),sQuery(id+"F0.wireOp",EDGE,"E27.MirrorCS"),sQuery(id+"F0.wireOp",EDGE,"E28.MirrorCS"),sQuery(id+"F0.wireOp",EDGE,"E29.MirrorCS"),sQuery(id+"F0.wireOp",EDGE,"E30.MirrorCS"),sQuery(id+"F0.wireOp",EDGE,"E31"),sQuery(id+"F0.wireOp",EDGE,"E32.MirrorCS"),sQuery(id+"F0.wireOp",EDGE,"E33.MirrorCS"),sQuery(id+"F0.wireOp",EDGE,"E34.MirrorCS"),sQuery(id+"F0.wireOp",EDGE,"E35.MirrorCS"),sQuery(id+"F0.wireOp",EDGE,"E36"),sQuery(id+"F0.wireOp",EDGE,"E37.bottom"),sQuery(id+"F0.wireOp",EDGE,"E37.top"),subQ0,sQuery(id+"F0.wireOp",EDGE,"E37.right"),sQuery(id+"F0.wireOp",EDGE,"E38.filletArc"),sQuery(id+"F0.wireOp",EDGE,"E39.filletArc"),sQuery(id+"F0.wireOp",EDGE,"E40.filletArc"),sQuery(id+"F0.wireOp",EDGE,"E41.filletArc"),sQuery(id+"F0.wireOp",EDGE,"E42.MirrorCS"),sQuery(id+"F0.wireOp",EDGE,"E43.MirrorCS"),sQuery(id+"F0.wireOp",EDGE,"E44.MirrorCS"),sQuery(id+"F0.wireOp",EDGE,"E45.MirrorCS"),sQuery(id+"F0.wireOp",EDGE,"E46.MirrorCS"),sQuery(id+"F0.wireOp",EDGE,"E47.MirrorCS"),sQuery(id+"F0.wireOp",EDGE,"E48.MirrorCS"),sQuery(id+"F0.wireOp",EDGE,"E49.MirrorCS"),sQuery(id+"F0.wireOp",EDGE,"E50"),sQuery(id+"F0.wireOp",EDGE,"E51.trimOffspring"),sQuery(id+"F0.wireOp",EDGE,"E52"),sQuery(id+"F0.wireOp",EDGE,"b30a117b-d75a-4502-b387-7b125c7515d1.trimOffspring"),sQuery(id+"F0.wireOp",EDGE,"E53"),sQuery(id+"F0.wireOp",EDGE,"E54.MirrorCS"),sQuery(id+"F0.wireOp",EDGE,"E55.trimOffspring"),sQuery(id+"F0.wireOp",EDGE,"E56.trimOffspring"),sQuery(id+"F0.wireOp",EDGE,"E57.trimOffspring"),sQuery(id+"F0.wireOp",EDGE,"XfeBEER9-2g1J-kN3v-mQVF-R0Wur47D0a7y"),sQuery(id+"F0.wireOp",EDGE,"cj9tdcR5-JuoR-tGsP-MGoO-S5KOOCOVeEPM"),sQuery(id+"F0.wireOp",EDGE,"E58.MirrorCS"),sQuery(id+"F0.wireOp",EDGE,"E59.MirrorCS"),sQuery(id+"F0.wireOp",EDGE,"c64e98b8-e32c-4987-8556-cb4b40954b380.MirrorCS"),sQuery(id+"F0.wireOp",EDGE,"E60.MirrorCS"),sQuery(id+"F0.wireOp",EDGE,"E61.MirrorCS"),sQuery(id+"F0.wireOp",EDGE,"E62.MirrorCS"),sQuery(id+"F0.wireOp",EDGE,"E63.MirrorCS"),sQuery(id+"F0.wireOp",EDGE,"bcf6c320-8a54-4c53-9ffd-94a113f5b3590.MirrorCS"),sQuery(id+"F0.wireOp",EDGE,"c17ce9da-a2d4-493a-92bd-da0e6258ab510.MirrorCS"),sQuery(id+"F0.wireOp",EDGE,"E64.MirrorCS"),sQuery(id+"F0.wireOp",EDGE,"E65.MirrorCS"),sQuery(id+"F0.wireOp",EDGE,"E66.MirrorCS"),sQuery(id+"F0.wireOp",EDGE,"eab108b2-96d9-45b4-925c-b77b0fad8b6b0.MirrorCS"),sQuery(id+"F0.wireOp",EDGE,"861f5b8e-cbd1-41e1-b2bb-9c07049055a20.MirrorCS")])],"isStart":true})],"blendedInto":[makeQuery(id+"F1.opExtrude","CAP_FACE",FACE,{"disambiguationData":[OSD([sQuery(id+"F0.wireOp",EDGE,"E1"),sQuery(id+"F0.wireOp",EDGE,"E2.MirrorC"),sQuery(id+"F0.wireOp",EDGE,"E3.MirrorC"),sQuery(id+"F0.wireOp",EDGE,"E4.MirrorC"),sQuery(id+"F0.wireOp",EDGE,"E5"),sQuery(id+"F0.wireOp",EDGE,"E6"),sQuery(id+"F0.wireOp",EDGE,"E7.MirrorC"),sQuery(id+"F0.wireOp",EDGE,"E8.MirrorC"),sQuery(id+"F0.wireOp",EDGE,"E9.MirrorC"),sQuery(id+"F0.wireOp",EDGE,"E11.MirrorCS"),sQuery(id+"F0.wireOp",EDGE,"E12.MirrorCS"),sQuery(id+"F0.wireOp",EDGE,"E13"),sQuery(id+"F0.wireOp",EDGE,"E14"),sQuery(id+"F0.wireOp",EDGE,"E15.MirrorCS"),sQuery(id+"F0.wireOp",EDGE,"E16.MirrorCS"),sQuery(id+"F0.wireOp",EDGE,"E17.MirrorCS"),sQuery(id+"F0.wireOp",EDGE,"E18.MirrorCS"),sQuery(id+"F0.wireOp",EDGE,"E19"),sQuery(id+"F0.wireOp",EDGE,"E20"),sQuery(id+"F0.wireOp",EDGE,"E21.MirrorCS"),sQuery(id+"F0.wireOp",EDGE,"E22.MirrorCS"),sQuery(id+"F0.wireOp",EDGE,"E23.MirrorCS"),sQuery(id+"F0.wireOp",EDGE,"E24.MirrorCS"),sQuery(id+"F0.wireOp",EDGE,"E25.MirrorCS"),sQuery(id+"F0.wireOp",EDGE,"E26.MirrorCS"),sQuery(id+"F0.wireOp",EDGE,"E27.MirrorCS"),sQuery(id+"F0.wireOp",EDGE,"E28.MirrorCS"),sQuery(id+"F0.wireOp",EDGE,"E29.MirrorCS"),sQuery(id+"F0.wireOp",EDGE,"E30.MirrorCS"),sQuery(id+"F0.wireOp",EDGE,"E31"),sQuery(id+"F0.wireOp",EDGE,"E32.MirrorCS"),sQuery(id+"F0.wireOp",EDGE,"E33.MirrorCS"),sQuery(id+"F0.wireOp",EDGE,"E34.MirrorCS"),sQuery(id+"F0.wireOp",EDGE,"E35.MirrorCS"),sQuery(id+"F0.wireOp",EDGE,"E36"),sQuery(id+"F0.wireOp",EDGE,"E37.bottom"),sQuery(id+"F0.wireOp",EDGE,"E37.top"),subQ0,sQuery(id+"F0.wireOp",EDGE,"E37.right"),sQuery(id+"F0.wireOp",EDGE,"E38.filletArc"),sQuery(id+"F0.wireOp",EDGE,"E39.filletArc"),sQuery(id+"F0.wireOp",EDGE,"E40.filletArc"),sQuery(id+"F0.wireOp",EDGE,"E41.filletArc"),sQuery(id+"F0.wireOp",EDGE,"E42.MirrorCS"),sQuery(id+"F0.wireOp",EDGE,"E43.MirrorCS"),sQuery(id+"F0.wireOp",EDGE,"E44.MirrorCS"),sQuery(id+"F0.wireOp",EDGE,"E45.MirrorCS"),sQuery(id+"F0.wireOp",EDGE,"E46.MirrorCS"),sQuery(id+"F0.wireOp",EDGE,"E47.MirrorCS"),sQuery(id+"F0.wireOp",EDGE,"E48.MirrorCS"),sQuery(id+"F0.wireOp",EDGE,"E49.MirrorCS"),sQuery(id+"F0.wireOp",EDGE,"E50"),sQuery(id+"F0.wireOp",EDGE,"E51.trimOffspring"),sQuery(id+"F0.wireOp",EDGE,"E52"),sQuery(id+"F0.wireOp",EDGE,"b30a117b-d75a-4502-b387-7b125c7515d1.trimOffspring"),sQuery(id+"F0.wireOp",EDGE,"E53"),sQuery(id+"F0.wireOp",EDGE,"E54.MirrorCS"),sQuery(id+"F0.wireOp",EDGE,"E55.trimOffspring"),sQuery(id+"F0.wireOp",EDGE,"E56.trimOffspring"),sQuery(id+"F0.wireOp",EDGE,"E57.trimOffspring"),sQuery(id+"F0.wireOp",EDGE,"XfeBEER9-2g1J-kN3v-mQVF-R0Wur47D0a7y"),sQuery(id+"F0.wireOp",EDGE,"cj9tdcR5-JuoR-tGsP-MGoO-S5KOOCOVeEPM"),sQuery(id+"F0.wireOp",EDGE,"E58.MirrorCS"),sQuery(id+"F0.wireOp",EDGE,"E59.MirrorCS"),sQuery(id+"F0.wireOp",EDGE,"c64e98b8-e32c-4987-8556-cb4b40954b380.MirrorCS"),sQuery(id+"F0.wireOp",EDGE,"E60.MirrorCS"),sQuery(id+"F0.wireOp",EDGE,"E61.MirrorCS"),sQuery(id+"F0.wireOp",EDGE,"E62.MirrorCS"),sQuery(id+"F0.wireOp",EDGE,"E63.MirrorCS"),sQuery(id+"F0.wireOp",EDGE,"bcf6c320-8a54-4c53-9ffd-94a113f5b3590.MirrorCS"),sQuery(id+"F0.wireOp",EDGE,"c17ce9da-a2d4-493a-92bd-da0e6258ab510.MirrorCS"),sQuery(id+"F0.wireOp",EDGE,"E64.MirrorCS"),sQuery(id+"F0.wireOp",EDGE,"E65.MirrorCS"),sQuery(id+"F0.wireOp",EDGE,"E66.MirrorCS"),sQuery(id+"F0.wireOp",EDGE,"eab108b2-96d9-45b4-925c-b77b0fad8b6b0.MirrorCS"),sQuery(id+"F0.wireOp",EDGE,"861f5b8e-cbd1-41e1-b2bb-9c07049055a20.MirrorCS")])],"isStart":true})]});}
            var Q20;
            Q20=makeQuery(id+"F1.opExtrude","CAP_EDGE",EDGE,{"disambiguationData":[OSD([sQuery(id+"F0.wireOp",EDGE,"E50")])],"isStart":true});
            var Q21;
            Q21=makeQuery(id+"F1.opExtrude","CAP_EDGE",EDGE,{"disambiguationData":[OSD([sQuery(id+"F0.wireOp",EDGE,"E36")])],"isStart":true});
            var Q22;
            Q22=makeQuery(id+"F1.opExtrude","CAP_EDGE",EDGE,{"disambiguationData":[OSD([sQuery(id+"F0.wireOp",EDGE,"E33.MirrorCS")])],"isStart":true});
            var Q23;
            Q23=makeQuery(id+"F1.opExtrude","CAP_EDGE",EDGE,{"disambiguationData":[OSD([sQuery(id+"F0.wireOp",EDGE,"E31")])],"isStart":true});
            var Q24;
            Q24=makeQuery(id+"F1.opExtrude","CAP_EDGE",EDGE,{"disambiguationData":[OSD([sQuery(id+"F0.wireOp",EDGE,"E1")])],"isStart":true});
            var Q25;
            Q25=makeQuery(id+"F1.opExtrude","CAP_EDGE",EDGE,{"disambiguationData":[OSD([sQuery(id+"F0.wireOp",EDGE,"E5")])],"isStart":true});
            var Q26;
            Q26=makeQuery(id+"F1.opExtrude","CAP_EDGE",EDGE,{"disambiguationData":[OSD([sQuery(id+"F0.wireOp",EDGE,"E51.trimOffspring")])],"isStart":true});
            var Q27;
            Q27=makeQuery(id+"F1.opExtrude","CAP_EDGE",EDGE,{"disambiguationData":[OSD([sQuery(id+"F0.wireOp",EDGE,"E55.trimOffspring")])],"isStart":true});
            var Q28;
            Q28=makeQuery(id+"F1.opExtrude","CAP_EDGE",EDGE,{"disambiguationData":[OSD([sQuery(id+"F0.wireOp",EDGE,"E2.MirrorC")])],"isStart":true});
            fillet(context, id + "F9", {"entities" : qUnion([Q0, Q1, Q2, Q3, Q4, Q5, Q6, Q7, Q8, Q9, Q10, Q11, Q12, Q13, Q14, Q15, Q16, Q17, Q18, Q19, Q20, Q21, Q22, Q23, Q24, Q25, Q26, Q27, Q28]), "radius" : .5 * mm, "tangentPropagation" : true, "allowEdgeOverflow" : false});
        }
        {
            var Q0;
            Q0=makeQuery(id+"F1.opExtrude","CAP_FACE",FACE,{"disambiguationData":[OSD([sQuery(id+"F0.wireOp",EDGE,"E1"),sQuery(id+"F0.wireOp",EDGE,"E2.MirrorC"),sQuery(id+"F0.wireOp",EDGE,"E3.MirrorC"),sQuery(id+"F0.wireOp",EDGE,"E4.MirrorC"),sQuery(id+"F0.wireOp",EDGE,"E5"),sQuery(id+"F0.wireOp",EDGE,"E6"),sQuery(id+"F0.wireOp",EDGE,"E7.MirrorC"),sQuery(id+"F0.wireOp",EDGE,"E8.MirrorC"),sQuery(id+"F0.wireOp",EDGE,"E9.MirrorC"),sQuery(id+"F0.wireOp",EDGE,"E11.MirrorCS"),sQuery(id+"F0.wireOp",EDGE,"E12.MirrorCS"),sQuery(id+"F0.wireOp",EDGE,"E13"),sQuery(id+"F0.wireOp",EDGE,"E14"),sQuery(id+"F0.wireOp",EDGE,"E15.MirrorCS"),sQuery(id+"F0.wireOp",EDGE,"E16.MirrorCS"),sQuery(id+"F0.wireOp",EDGE,"E17.MirrorCS"),sQuery(id+"F0.wireOp",EDGE,"E18.MirrorCS"),sQuery(id+"F0.wireOp",EDGE,"E19"),sQuery(id+"F0.wireOp",EDGE,"E20"),sQuery(id+"F0.wireOp",EDGE,"E21.MirrorCS"),sQuery(id+"F0.wireOp",EDGE,"E22.MirrorCS"),sQuery(id+"F0.wireOp",EDGE,"E23.MirrorCS"),sQuery(id+"F0.wireOp",EDGE,"E24.MirrorCS"),sQuery(id+"F0.wireOp",EDGE,"E25.MirrorCS"),sQuery(id+"F0.wireOp",EDGE,"E26.MirrorCS"),sQuery(id+"F0.wireOp",EDGE,"E27.MirrorCS"),sQuery(id+"F0.wireOp",EDGE,"E28.MirrorCS"),sQuery(id+"F0.wireOp",EDGE,"E29.MirrorCS"),sQuery(id+"F0.wireOp",EDGE,"E30.MirrorCS"),sQuery(id+"F0.wireOp",EDGE,"E31"),sQuery(id+"F0.wireOp",EDGE,"E32.MirrorCS"),sQuery(id+"F0.wireOp",EDGE,"E33.MirrorCS"),sQuery(id+"F0.wireOp",EDGE,"E34.MirrorCS"),sQuery(id+"F0.wireOp",EDGE,"E35.MirrorCS"),sQuery(id+"F0.wireOp",EDGE,"E36"),sQuery(id+"F0.wireOp",EDGE,"E37.bottom"),sQuery(id+"F0.wireOp",EDGE,"E37.top"),sQuery(id+"F0.wireOp",EDGE,"E37.left"),sQuery(id+"F0.wireOp",EDGE,"E37.right"),sQuery(id+"F0.wireOp",EDGE,"E38.filletArc"),sQuery(id+"F0.wireOp",EDGE,"E39.filletArc"),sQuery(id+"F0.wireOp",EDGE,"E40.filletArc"),sQuery(id+"F0.wireOp",EDGE,"E41.filletArc"),sQuery(id+"F0.wireOp",EDGE,"E42.MirrorCS"),sQuery(id+"F0.wireOp",EDGE,"E43.MirrorCS"),sQuery(id+"F0.wireOp",EDGE,"E44.MirrorCS"),sQuery(id+"F0.wireOp",EDGE,"E45.MirrorCS"),sQuery(id+"F0.wireOp",EDGE,"E46.MirrorCS"),sQuery(id+"F0.wireOp",EDGE,"E47.MirrorCS"),sQuery(id+"F0.wireOp",EDGE,"E48.MirrorCS"),sQuery(id+"F0.wireOp",EDGE,"E49.MirrorCS"),sQuery(id+"F0.wireOp",EDGE,"E50"),sQuery(id+"F0.wireOp",EDGE,"E51.trimOffspring"),sQuery(id+"F0.wireOp",EDGE,"E52"),sQuery(id+"F0.wireOp",EDGE,"b30a117b-d75a-4502-b387-7b125c7515d1.trimOffspring"),sQuery(id+"F0.wireOp",EDGE,"E53"),sQuery(id+"F0.wireOp",EDGE,"E54.MirrorCS"),sQuery(id+"F0.wireOp",EDGE,"E55.trimOffspring"),sQuery(id+"F0.wireOp",EDGE,"E56.trimOffspring"),sQuery(id+"F0.wireOp",EDGE,"E57.trimOffspring"),sQuery(id+"F0.wireOp",EDGE,"XfeBEER9-2g1J-kN3v-mQVF-R0Wur47D0a7y"),sQuery(id+"F0.wireOp",EDGE,"cj9tdcR5-JuoR-tGsP-MGoO-S5KOOCOVeEPM"),sQuery(id+"F0.wireOp",EDGE,"E58.MirrorCS"),sQuery(id+"F0.wireOp",EDGE,"E59.MirrorCS"),sQuery(id+"F0.wireOp",EDGE,"c64e98b8-e32c-4987-8556-cb4b40954b380.MirrorCS"),sQuery(id+"F0.wireOp",EDGE,"E60.MirrorCS"),sQuery(id+"F0.wireOp",EDGE,"E61.MirrorCS"),sQuery(id+"F0.wireOp",EDGE,"E62.MirrorCS"),sQuery(id+"F0.wireOp",EDGE,"E63.MirrorCS"),sQuery(id+"F0.wireOp",EDGE,"bcf6c320-8a54-4c53-9ffd-94a113f5b3590.MirrorCS"),sQuery(id+"F0.wireOp",EDGE,"c17ce9da-a2d4-493a-92bd-da0e6258ab510.MirrorCS"),sQuery(id+"F0.wireOp",EDGE,"E64.MirrorCS"),sQuery(id+"F0.wireOp",EDGE,"E65.MirrorCS"),sQuery(id+"F0.wireOp",EDGE,"E66.MirrorCS"),sQuery(id+"F0.wireOp",EDGE,"eab108b2-96d9-45b4-925c-b77b0fad8b6b0.MirrorCS"),sQuery(id+"F0.wireOp",EDGE,"861f5b8e-cbd1-41e1-b2bb-9c07049055a20.MirrorCS")])],"isStart":false});
            var sketch = newSketch(context, id + "F10", { "sketchPlane" : qUnion([Q0])});
            skPoint(sketch, "E104", {"position": v(17.08, -38.68) * mm});
            skPoint(sketch, "E105", {"position": v(19.36, -40.8) * mm});
            skArc(sketch, "E106", {"start": v(17.08, -38.68) * mm, "mid": v(18.16, -39.8) * mm, "end": v(19.36, -40.8) * mm});
            skPoint(sketch, "E107", {"position": v(17.34, -42.89) * mm});
            skPoint(sketch, "E108", {"position": v(15.3, -41.07) * mm});
            skArc(sketch, "E109", {"start": v(17.34, -42.89) * mm, "mid": v(16.68, -41.58) * mm, "end": v(15.3, -41.07) * mm});
            skPoint(sketch, "E110.right.end.orphan", {"position": v(13.51, -37.55) * mm});
            skArc(sketch, "E111", {"start": v(17.08, -38.68) * mm, "mid": v(14.83, -38.87) * mm, "end": v(15.3, -41.07) * mm});
            skArc(sketch, "E112", {"start": v(17.34, -42.89) * mm, "mid": v(19.54, -43.3) * mm, "end": v(19.71, -41.08) * mm});
            skPoint(sketch, "E113", {"position": v(19.71, -41.08) * mm});
            skLineSegment(sketch, "E114", {"start": v(19.71, -41.08) * mm, "end": v(19.36, -40.8) * mm});
            skArc(sketch, "E115.MirrorCS", {"start": v(-17.08, -38.68) * mm, "mid": v(-14.83, -38.87) * mm, "end": v(-15.3, -41.07) * mm});
            skArc(sketch, "E116.MirrorCS", {"start": v(-17.08, -38.68) * mm, "mid": v(-18.16, -39.8) * mm, "end": v(-19.36, -40.8) * mm});
            skLineSegment(sketch, "E117.MirrorCS", {"start": v(-19.71, -41.08) * mm, "end": v(-19.36, -40.8) * mm});
            skArc(sketch, "E118.MirrorCS", {"start": v(-17.34, -42.89) * mm, "mid": v(-19.54, -43.3) * mm, "end": v(-19.71, -41.08) * mm});
            skArc(sketch, "E119.MirrorCS", {"start": v(-17.34, -42.89) * mm, "mid": v(-16.68, -41.58) * mm, "end": v(-15.3, -41.07) * mm});
            skArc(sketch, "E120.MirrorCS", {"start": v(-17.08, 38.68) * mm, "mid": v(-14.83, 38.87) * mm, "end": v(-15.3, 41.07) * mm});
            skArc(sketch, "E121.MirrorCS", {"start": v(-17.34, 42.89) * mm, "mid": v(-16.68, 41.58) * mm, "end": v(-15.3, 41.07) * mm});
            skArc(sketch, "E122.MirrorCS", {"start": v(-17.34, 42.89) * mm, "mid": v(-19.54, 43.3) * mm, "end": v(-19.71, 41.08) * mm});
            skArc(sketch, "E123.MirrorCS", {"start": v(-17.08, 38.68) * mm, "mid": v(-18.16, 39.8) * mm, "end": v(-19.36, 40.8) * mm});
            skLineSegment(sketch, "E124.MirrorCS", {"start": v(-19.71, 41.08) * mm, "end": v(-19.36, 40.8) * mm});
            skArc(sketch, "E125.MirrorCS", {"start": v(17.08, 38.68) * mm, "mid": v(18.16, 39.8) * mm, "end": v(19.36, 40.8) * mm});
            skArc(sketch, "E126.MirrorCS", {"start": v(17.08, 38.68) * mm, "mid": v(14.83, 38.87) * mm, "end": v(15.3, 41.07) * mm});
            skArc(sketch, "E127.MirrorCS", {"start": v(17.34, 42.89) * mm, "mid": v(16.68, 41.58) * mm, "end": v(15.3, 41.07) * mm});
            skArc(sketch, "E128.MirrorCS", {"start": v(17.34, 42.89) * mm, "mid": v(19.54, 43.3) * mm, "end": v(19.71, 41.08) * mm});
            skLineSegment(sketch, "E129.MirrorCS", {"start": v(19.71, 41.08) * mm, "end": v(19.36, 40.8) * mm});
            skLineSegment(sketch, "E130", {"start": v(16.68, -41.58) * mm, "end": v(18.16, -39.8) * mm, "construction": true});
            skSolve(sketch);
        }
        {
            var Q0;
            Q0=qSketchRegion(id+"F10",true);
            extrude(context, id + "F11", {"entities" : qUnion([Q0]), "operationType" : NewBodyOperationType.ADD, "depth" : 1 * mm});
        }
        {
            var Q0;
            Q0=makeQuery(id+"F11.opExtrude","CAP_EDGE",EDGE,{"disambiguationData":[OSD([sQuery(id+"F10.wireOp",EDGE,"E109")])],"isStart":false});
            var Q1;
            Q1=makeQuery(id+"F11.opExtrude","CAP_EDGE",EDGE,{"disambiguationData":[OSD([sQuery(id+"F10.wireOp",EDGE,"E111")])],"isStart":false});
            var Q2;
            Q2=makeQuery(id+"F11.opExtrude","CAP_EDGE",EDGE,{"disambiguationData":[OSD([sQuery(id+"F10.wireOp",EDGE,"E106")])],"isStart":false});
            var Q3;
            Q3=makeQuery(id+"F11.opExtrude","CAP_EDGE",EDGE,{"disambiguationData":[OSD([sQuery(id+"F10.wireOp",EDGE,"E112")])],"isStart":false});
            var Q4;
            Q4=makeQuery(id+"F11.opExtrude","CAP_EDGE",EDGE,{"disambiguationData":[OSD([sQuery(id+"F10.wireOp",EDGE,"E114")])],"isStart":false});
            var Q5;
            Q5=makeQuery(id+"F11.opExtrude","CAP_EDGE",EDGE,{"disambiguationData":[OSD([sQuery(id+"F10.wireOp",EDGE,"E118.MirrorCS")])],"isStart":false});
            var Q6;
            Q6=makeQuery(id+"F11.opExtrude","CAP_EDGE",EDGE,{"disambiguationData":[OSD([sQuery(id+"F10.wireOp",EDGE,"E119.MirrorCS")])],"isStart":false});
            var Q7;
            Q7=makeQuery(id+"F11.opExtrude","CAP_EDGE",EDGE,{"disambiguationData":[OSD([sQuery(id+"F10.wireOp",EDGE,"E115.MirrorCS")])],"isStart":false});
            var Q8;
            Q8=makeQuery(id+"F11.opExtrude","CAP_EDGE",EDGE,{"disambiguationData":[OSD([sQuery(id+"F10.wireOp",EDGE,"E116.MirrorCS")])],"isStart":false});
            var Q9;
            Q9=makeQuery(id+"F11.opExtrude","CAP_EDGE",EDGE,{"disambiguationData":[OSD([sQuery(id+"F10.wireOp",EDGE,"E117.MirrorCS")])],"isStart":false});
            var Q10;
            Q10=makeQuery(id+"F11.opExtrude","CAP_EDGE",EDGE,{"disambiguationData":[OSD([sQuery(id+"F10.wireOp",EDGE,"E123.MirrorCS")])],"isStart":false});
            var Q11;
            Q11=makeQuery(id+"F11.opExtrude","CAP_EDGE",EDGE,{"disambiguationData":[OSD([sQuery(id+"F10.wireOp",EDGE,"E124.MirrorCS")])],"isStart":false});
            var Q12;
            Q12=makeQuery(id+"F11.opExtrude","CAP_EDGE",EDGE,{"disambiguationData":[OSD([sQuery(id+"F10.wireOp",EDGE,"E122.MirrorCS")])],"isStart":false});
            var Q13;
            Q13=makeQuery(id+"F11.opExtrude","CAP_EDGE",EDGE,{"disambiguationData":[OSD([sQuery(id+"F10.wireOp",EDGE,"E121.MirrorCS")])],"isStart":false});
            var Q14;
            Q14=makeQuery(id+"F11.opExtrude","CAP_EDGE",EDGE,{"disambiguationData":[OSD([sQuery(id+"F10.wireOp",EDGE,"E120.MirrorCS")])],"isStart":false});
            var Q15;
            Q15=makeQuery(id+"F11.opExtrude","CAP_EDGE",EDGE,{"disambiguationData":[OSD([sQuery(id+"F10.wireOp",EDGE,"E125.MirrorCS")])],"isStart":false});
            var Q16;
            Q16=makeQuery(id+"F11.opExtrude","CAP_EDGE",EDGE,{"disambiguationData":[OSD([sQuery(id+"F10.wireOp",EDGE,"E129.MirrorCS")])],"isStart":false});
            var Q17;
            Q17=makeQuery(id+"F11.opExtrude","CAP_EDGE",EDGE,{"disambiguationData":[OSD([sQuery(id+"F10.wireOp",EDGE,"E128.MirrorCS")])],"isStart":false});
            var Q18;
            Q18=makeQuery(id+"F11.opExtrude","CAP_EDGE",EDGE,{"disambiguationData":[OSD([sQuery(id+"F10.wireOp",EDGE,"E127.MirrorCS")])],"isStart":false});
            var Q19;
            Q19=makeQuery(id+"F11.opExtrude","CAP_EDGE",EDGE,{"disambiguationData":[OSD([sQuery(id+"F10.wireOp",EDGE,"E126.MirrorCS")])],"isStart":false});
            fillet(context, id + "F12", {"entities" : qUnion([Q0, Q1, Q2, Q3, Q4, Q5, Q6, Q7, Q8, Q9, Q10, Q11, Q12, Q13, Q14, Q15, Q16, Q17, Q18, Q19]), "radius" : 1 * mm, "tangentPropagation" : true, "allowEdgeOverflow" : false});
        }
    });
